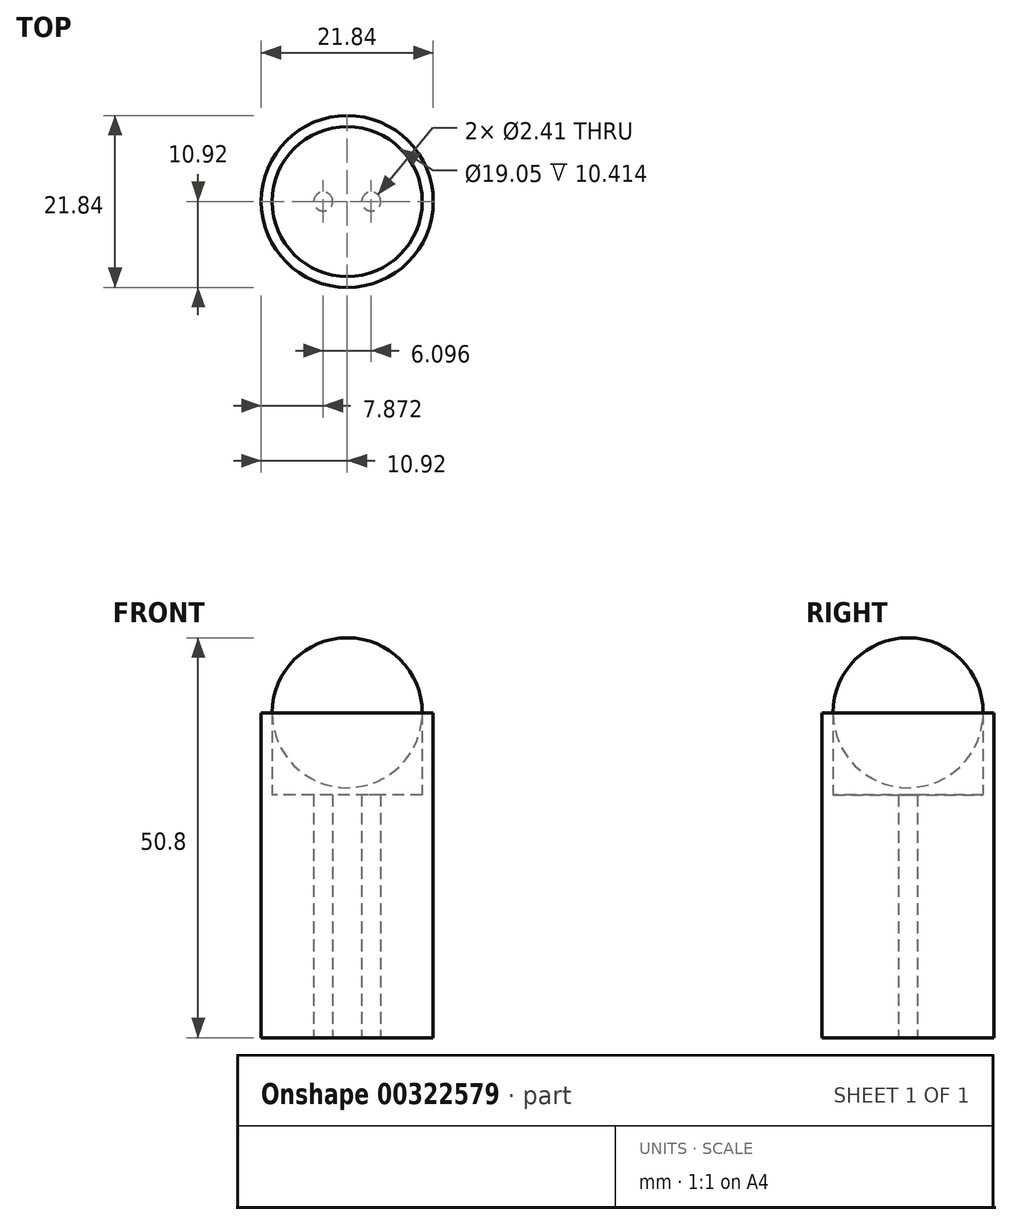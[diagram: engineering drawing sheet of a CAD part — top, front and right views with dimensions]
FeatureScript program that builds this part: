
annotation { "Feature Type Name" : "Feature", "Feature Type Description" : "" }
export const myFeature = defineFeature(function(context is Context, id is Id, definition is map)
    precondition{}
    {
        {
            var Q0;
            Q0=qCreatedBy(makeId("Top.planeOp"),FACE);
            var sketch = newSketch(context, id + "F0", { "sketchPlane" : qUnion([Q0])});
            skCircle(sketch, "E0", {"center": v(0, 0) * mm, "radius": 10.92 * mm});
            skCircle(sketch, "E1", {"center": v(0, 0) * mm, "radius": 9.53 * mm});
            skSolve(sketch);
        }
        {
            var Q0;
            Q0=makeQuery(id+"F0.imprint","IMPRINT",FACE,{"disambiguationData":[TD([[makeQuery(id+"F0.imprint","IMPRINT",EDGE,{"derivedFrom":sQuery(id+"F0.wireOp",EDGE,"E0")}),1.0]])]});
            extrude(context, id + "F1", {"entities" : qUnion([Q0]), "depth" : 13.6 * mm, "offsetDistance" : 25.4 * mm});
        }
        {
            var Q0;
            Q0=makeQuery(id+"F1.opExtrude","CAP_FACE",FACE,{"disambiguationData":[OSD([sQuery(id+"F0.wireOp",EDGE,"E0")])],"isStart":false});
            var sketch = newSketch(context, id + "F2", { "sketchPlane" : qUnion([Q0])});
            skLineSegment(sketch, "E2", {"start": v(-20.82, 0) * mm, "end": v(35.75, 0) * mm, "construction": true});
            skArc(sketch, "E3", {"start": v(-9.53, 0) * mm, "mid": v(0, -9.53) * mm, "end": v(9.53, 0) * mm});
            skLineSegment(sketch, "E4", {"start": v(-9.53, 0) * mm, "end": v(9.53, 0) * mm});
            skSolve(sketch);
        }
        {
            var Q0;
            Q0=makeQuery(id+"F2.imprint","IMPRINT",FACE,{"disambiguationData":[TD([[makeQuery(id+"F2.imprint","IMPRINT",EDGE,{"derivedFrom":sQuery(id+"F2.wireOp",EDGE,"E3")}),1.0]])]});
            var Q1;
            Q1=sQuery(id+"F2.wireOp",EDGE,"E2");
            revolve(context, id + "F3", {"entities" : qUnion([Q0]), "axis" : qUnion([Q1]), "revolveType" : RevolveType.FULL, "oppositeDirection" : true});
        }
        {
            var Q0;
            Q0=qCreatedBy(makeId("Top.planeOp"),FACE);
            var sketch = newSketch(context, id + "F4", { "sketchPlane" : qUnion([Q0])});
            skCircle(sketch, "E5", {"center": v(0, 0) * mm, "radius": 9.53 * mm});
            skCircle(sketch, "E6", {"center": v(3.05, 0) * mm, "radius": 1.2 * mm});
            skCircle(sketch, "E7.MirrorC", {"center": v(-3.05, 0) * mm, "radius": 1.2 * mm});
            skSolve(sketch);
        }
        {
            var Q0;
            Q0=qSketchRegion(id+"F4",true);
            extrude(context, id + "F5", {"entities" : qUnion([Q0]), "operationType" : NewBodyOperationType.ADD, "depth" : 3.17 * mm, "offsetDistance" : 25.4 * mm});
        }
        {
            var Q0;
            Q0=makeQuery(id+"F5.boolean.opBoolean","MERGE",FACE,{"derivedFrom":[makeQuery(id+"F1.opExtrude","CAP_FACE",FACE,{"disambiguationData":[OSD([sQuery(id+"F0.wireOp",EDGE,"E0"),sQuery(id+"F0.wireOp",EDGE,"E1")])],"isStart":true}),makeQuery(id+"F5.opExtrude","CAP_FACE",FACE,{"disambiguationData":[OSD([sQuery(id+"F4.wireOp",EDGE,"E5"),sQuery(id+"F4.wireOp",EDGE,"E6"),sQuery(id+"F4.wireOp",EDGE,"E7.MirrorC")])],"isStart":true})]});
            extrude(context, id + "F6", {"entities" : qUnion([Q0]), "operationType" : NewBodyOperationType.ADD, "depth" : 27.7 * mm, "offsetDistance" : 25.4 * mm});
        }
    });
